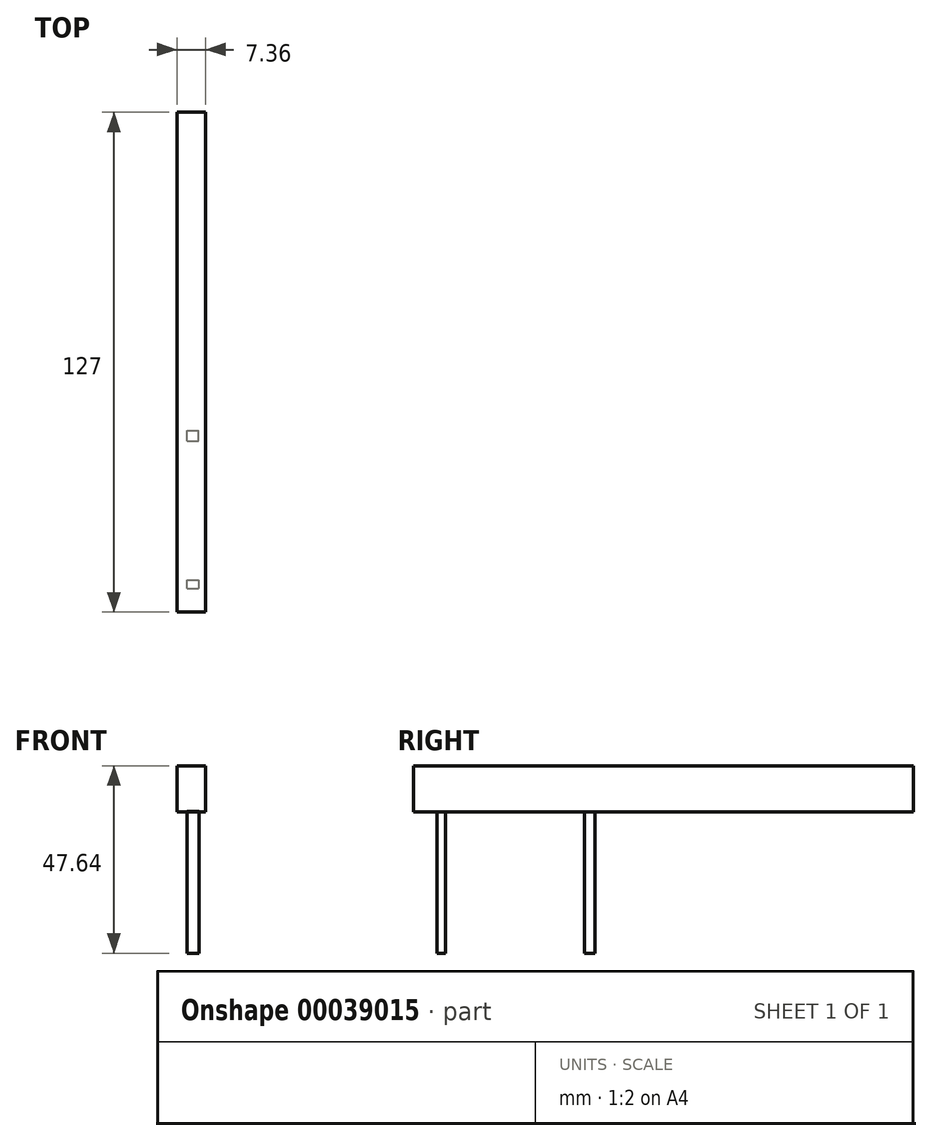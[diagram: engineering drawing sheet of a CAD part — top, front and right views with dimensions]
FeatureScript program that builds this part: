
annotation { "Feature Type Name" : "Feature", "Feature Type Description" : "" }
export const myFeature = defineFeature(function(context is Context, id is Id, definition is map)
    precondition{}
    {
        {
            var Q0;
            Q0=qCreatedBy(makeId("Front.planeOp"),FACE);
            var sketch = newSketch(context, id + "F0", { "sketchPlane" : qUnion([Q0])});
            skLineSegment(sketch, "E0.bottom", {"start": v(-47.64, 47.64) * mm, "end": v(-40.28, 47.64) * mm});
            skLineSegment(sketch, "E0.top", {"start": v(-47.64, 35.94) * mm, "end": v(-40.28, 35.94) * mm});
            skLineSegment(sketch, "E0.left", {"start": v(-47.64, 47.64) * mm, "end": v(-47.64, 35.94) * mm});
            skLineSegment(sketch, "E0.right", {"start": v(-40.28, 47.64) * mm, "end": v(-40.28, 35.94) * mm});
            skSolve(sketch);
        }
        {
            var Q0;
            Q0=sQuery(id+"F0.wireOp",EDGE,"E0.bottom");
            var Q1;
            Q1=sQuery(id+"F0.wireOp",EDGE,"E0.top");
            var Q2;
            Q2=sQuery(id+"F0.wireOp",EDGE,"E0.left");
            var Q3;
            Q3=sQuery(id+"F0.wireOp",EDGE,"E0.right");
            extrude(context, id + "F1", {"bodyType" : ToolBodyType.SURFACE, "surfaceEntities" : qUnion([Q0, Q1, Q2, Q3]), "endBound" : BoundingType.SYMMETRIC, "depth" : 127 * mm});
        }
        {
            var Q0;
            Q0=qCreatedBy(makeId("Top.planeOp"),FACE);
            var sketch = newSketch(context, id + "F2", { "sketchPlane" : qUnion([Q0])});
            skLineSegment(sketch, "E1.bottom", {"start": v(-45.07, -57.5) * mm, "end": v(-41.97, -57.5) * mm});
            skLineSegment(sketch, "E1.top", {"start": v(-45.07, -55.37) * mm, "end": v(-41.97, -55.37) * mm});
            skLineSegment(sketch, "E1.left", {"start": v(-45.07, -57.5) * mm, "end": v(-45.07, -55.37) * mm});
            skLineSegment(sketch, "E1.right", {"start": v(-41.97, -57.5) * mm, "end": v(-41.97, -55.37) * mm});
            skLineSegment(sketch, "E2.bottom", {"start": v(-45.09, -20.01) * mm, "end": v(-42.1, -20.01) * mm});
            skLineSegment(sketch, "E2.top", {"start": v(-45.09, -17.34) * mm, "end": v(-42.1, -17.34) * mm});
            skLineSegment(sketch, "E2.left", {"start": v(-45.09, -20.01) * mm, "end": v(-45.09, -17.34) * mm});
            skLineSegment(sketch, "E2.right", {"start": v(-42.1, -20.01) * mm, "end": v(-42.1, -17.34) * mm});
            skSolve(sketch);
        }
        {
            var Q0;
            Q0=sQuery(id+"F2.wireOp",EDGE,"E1.bottom");
            var Q1;
            Q1=sQuery(id+"F2.wireOp",EDGE,"E1.left");
            var Q2;
            Q2=sQuery(id+"F2.wireOp",EDGE,"E1.right");
            var Q3;
            Q3=sQuery(id+"F2.wireOp",EDGE,"E2.bottom");
            var Q4;
            Q4=sQuery(id+"F2.wireOp",EDGE,"E2.left");
            var Q5;
            Q5=sQuery(id+"F2.wireOp",EDGE,"E2.right");
            var Q6;
            Q6=sQuery(id+"F2.wireOp",EDGE,"E2.top");
            var Q7;
            Q7=sQuery(id+"F2.wireOp",EDGE,"E1.top");
            extrude(context, id + "F3", {"bodyType" : ToolBodyType.SURFACE, "surfaceEntities" : qUnion([Q0, Q1, Q2, Q3, Q4, Q5, Q6, Q7]), "depth" : 36.07 * mm});
        }
    });
